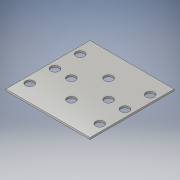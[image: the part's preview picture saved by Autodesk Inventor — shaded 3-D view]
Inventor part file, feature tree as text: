
AUTODESK INVENTOR PART (.ipt)
format: ipt  version: 2016 (Build 200138000, 138)  size: 166,912 bytes
history: native  units: mm
features: other x3, sketch x2, extrude x1, hole x1, projected_geometry x1
ambient origin geometry x8: Origin, YZ Plane, XZ Plane, XY Plane, X Axis, Y Axis, Z Axis, Center Point
bodies: Solid1 (feature_tree)
feature tree (8):
  other  "Blocks"
  extrude  "Extrusion1"  Depth=38.1mm
  hole  "Hole3"  [1 undecoded]
  sketch  "Sketch1"  dims[d0=38.1mm d1=38.1mm]
  sketch  "Sketch4"  dims[d2=0.79375mm d3=0.0mm d29=31.75mm d30=22.86mm d31=22.86mm d32=31.75mm d33=11.938mm d34=11.938mm d42=16.882882mm d43=16.882882mm d44=3.175mm d45=3.175mm d46=7.62mm d47=3.175mm d48=7.62mm d49=3.175mm d50=7.62mm d51=3.7973mm d52=19.05mm d53=9.525mm d54=6.35mm d55=14.3117mm d56=25.4mm d57=20.594885mm d58=4.445mm d59=7.433559mm d60=5.969mm d61=5.969mm d62=4.445mm d63=7.433559mm d64=9.906mm d65=9.906mm d66=15.875mm d67=5.969mm d68=21.844mm d69=21.844mm]
  projected_geometry  "Projected Loop2"
  other  "adapter-hole-geometry"
  other  "adapter-hole-geometry:1"
note: 1 required parameter value undecoded (feature->parameter linkage not recoverable at this tier; creation-order binding heuristic only, values carry confidence <= 0.55)
